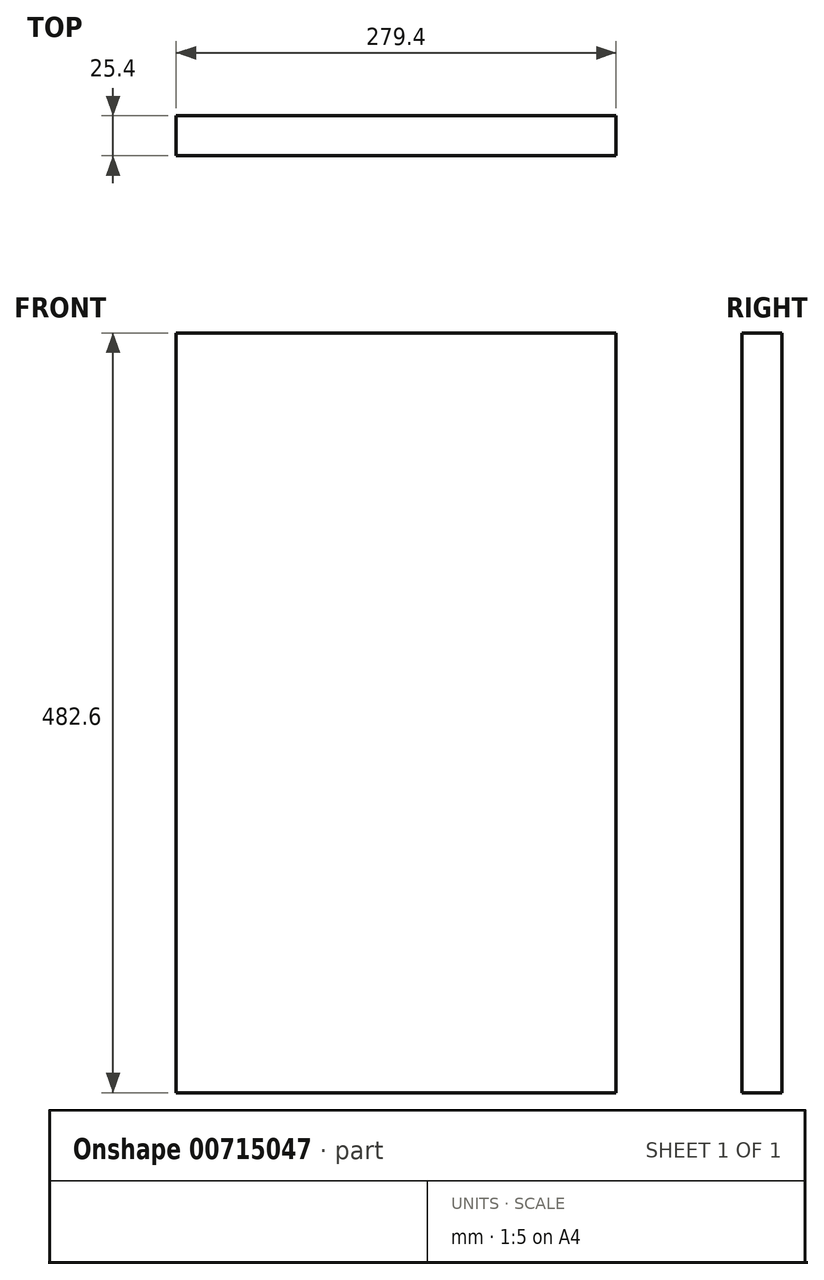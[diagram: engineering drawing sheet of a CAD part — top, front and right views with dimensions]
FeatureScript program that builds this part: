
annotation { "Feature Type Name" : "Feature", "Feature Type Description" : "" }
export const myFeature = defineFeature(function(context is Context, id is Id, definition is map)
    precondition{}
    {
        {
            var Q0;
            Q0=qCreatedBy(makeId("Front.planeOp"),FACE);
            var sketch = newSketch(context, id + "F0", { "sketchPlane" : qUnion([Q0])});
            skLineSegment(sketch, "E0.bottom", {"start": v(-172.32, -106.26) * mm, "end": v(107.08, -106.26) * mm});
            skLineSegment(sketch, "E0.top", {"start": v(-172.32, -588.86) * mm, "end": v(107.08, -588.86) * mm});
            skLineSegment(sketch, "E0.left", {"start": v(-172.32, -106.26) * mm, "end": v(-172.32, -588.86) * mm});
            skLineSegment(sketch, "E0.right", {"start": v(107.08, -106.26) * mm, "end": v(107.08, -588.86) * mm});
            skSolve(sketch);
        }
        {
            var Q0;
            Q0=makeQuery(id+"F0.imprint","IMPRINT",FACE,{"disambiguationData":[TD([[makeQuery(id+"F0.imprint","IMPRINT",EDGE,{"derivedFrom":sQuery(id+"F0.wireOp",EDGE,"E0.bottom")}),-1.0]])]});
            extrude(context, id + "F1", {"entities" : qUnion([Q0]), "depth" : 25.4 * mm, "offsetDistance" : 25.4 * mm});
        }
    });
